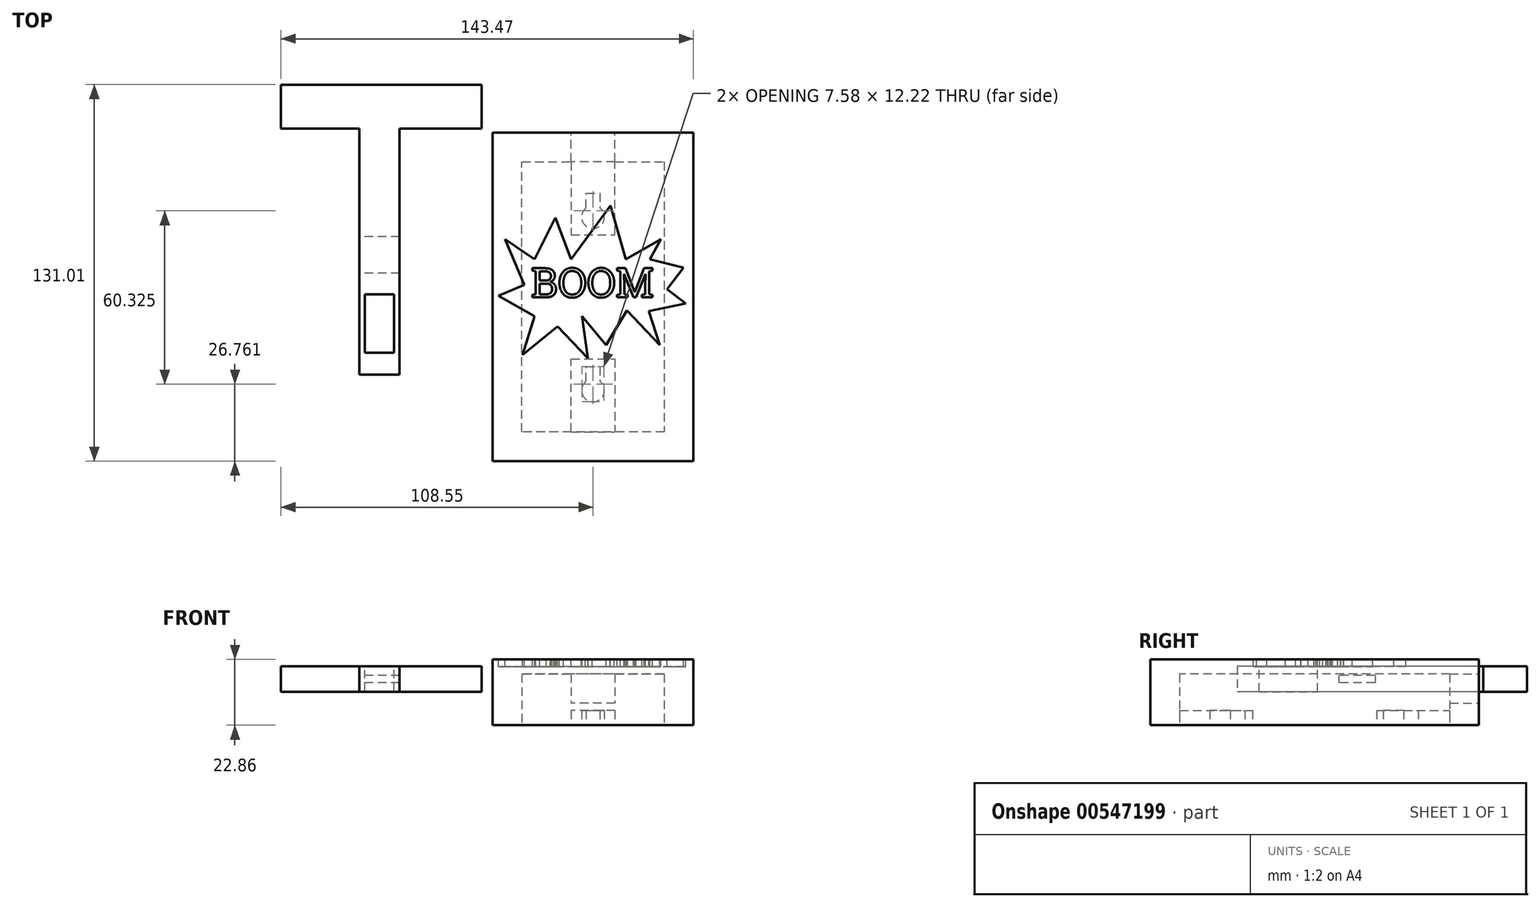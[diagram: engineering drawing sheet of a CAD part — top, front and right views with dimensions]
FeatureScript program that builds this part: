
annotation { "Feature Type Name" : "Feature", "Feature Type Description" : "" }
export const myFeature = defineFeature(function(context is Context, id is Id, definition is map)
    precondition{}
    {
        {
            var Q0;
            Q0=qCreatedBy(makeId("Top.planeOp"),FACE);
            var sketch = newSketch(context, id + "F0", { "sketchPlane" : qUnion([Q0])});
            skCircle(sketch, "E0", {"center": v(0, 34.46) * mm, "radius": 3.97 * mm});
            skCircle(sketch, "E1", {"center": v(0, -25.87) * mm, "radius": 3.97 * mm});
            skLineSegment(sketch, "E2", {"start": v(-34.92, 63.81) * mm, "end": v(34.93, 63.81) * mm});
            skLineSegment(sketch, "E3", {"start": v(34.93, 63.81) * mm, "end": v(34.93, -50.49) * mm});
            skLineSegment(sketch, "E4", {"start": v(34.93, -50.49) * mm, "end": v(-34.92, -50.49) * mm});
            skLineSegment(sketch, "E5", {"start": v(-34.92, -50.49) * mm, "end": v(-34.92, 63.81) * mm});
            skLineSegment(sketch, "E6", {"start": v(-24.76, -40.33) * mm, "end": v(-24.76, 53.65) * mm});
            skLineSegment(sketch, "E7", {"start": v(-24.76, 53.65) * mm, "end": v(24.77, 53.65) * mm});
            skLineSegment(sketch, "E8", {"start": v(24.77, 53.65) * mm, "end": v(24.77, -40.33) * mm});
            skLineSegment(sketch, "E9", {"start": v(24.77, -40.33) * mm, "end": v(-24.76, -40.33) * mm});
            skLineSegment(sketch, "E10", {"start": v(-2.39, 37.63) * mm, "end": v(-2.39, 42.7) * mm});
            skLineSegment(sketch, "E11", {"start": v(2.39, 42.7) * mm, "end": v(2.39, 37.63) * mm});
            skLineSegment(sketch, "E12", {"start": v(-2.39, 42.7) * mm, "end": v(0, 42.7) * mm});
            skLineSegment(sketch, "E13", {"start": v(0, 42.7) * mm, "end": v(2.39, 42.7) * mm});
            skLineSegment(sketch, "E14", {"start": v(-2.39, -22.7) * mm, "end": v(-2.39, -17.62) * mm});
            skLineSegment(sketch, "E15", {"start": v(-2.39, -17.62) * mm, "end": v(0, -17.62) * mm});
            skLineSegment(sketch, "E16", {"start": v(0, -17.62) * mm, "end": v(2.39, -17.62) * mm});
            skLineSegment(sketch, "E17", {"start": v(2.39, -17.62) * mm, "end": v(2.39, -22.7) * mm});
            skLineSegment(sketch, "E18", {"start": v(-7.62, 53.65) * mm, "end": v(-7.62, 28.25) * mm});
            skLineSegment(sketch, "E19", {"start": v(7.62, 28.25) * mm, "end": v(7.62, 53.65) * mm});
            skLineSegment(sketch, "E20", {"start": v(-7.62, 28.25) * mm, "end": v(0, 28.25) * mm});
            skLineSegment(sketch, "E21", {"start": v(0, 28.25) * mm, "end": v(7.62, 28.25) * mm});
            skLineSegment(sketch, "E22", {"start": v(-7.62, -40.33) * mm, "end": v(-7.62, -14.93) * mm});
            skLineSegment(sketch, "E23", {"start": v(-7.62, -14.93) * mm, "end": v(0, -14.93) * mm});
            skLineSegment(sketch, "E24", {"start": v(0, -14.93) * mm, "end": v(7.62, -14.93) * mm});
            skLineSegment(sketch, "E25", {"start": v(7.62, -14.93) * mm, "end": v(7.62, -40.33) * mm});
            skSolve(sketch);
        }
        {
            var Q0;
            Q0=makeQuery(id+"F0.imprint","IMPRINT",FACE,{"disambiguationData":[TD([[makeQuery(id+"F0.imprint","IMPRINT",EDGE,{"derivedFrom":sQuery(id+"F0.wireOp",EDGE,"E2")}),-1.0]])]});
            var Q1;
            {var subQ0=sQuery(id+"F0.wireOp",EDGE,"E14");Q1=makeQuery(id+"F0.imprint","IMPRINT",FACE,{"disambiguationData":[TD([[makeQuery(id+"F0.imprint","IMPRINT",EDGE,{"derivedFrom":subQ0}),1.0]])]});}
            var Q2;
            {var subQ4=sQuery(id+"F0.wireOp",EDGE,"E10");Q2=makeQuery(id+"F0.imprint","IMPRINT",FACE,{"disambiguationData":[TD([[makeQuery(id+"F0.imprint","IMPRINT",EDGE,{"derivedFrom":subQ4}),1.0]])]});}
            extrude(context, id + "F1", {"entities" : qUnion([Q0, Q1, Q2]), "depth" : 5.08 * mm});
        }
        {
            var Q0;
            Q0=makeQuery(id+"F0.imprint","IMPRINT",FACE,{"disambiguationData":[TD([[makeQuery(id+"F0.imprint","IMPRINT",EDGE,{"derivedFrom":sQuery(id+"F0.wireOp",EDGE,"E2")}),-1.0]])]});
            extrude(context, id + "F2", {"entities" : qUnion([Q0]), "operationType" : NewBodyOperationType.ADD, "depth" : 10.16 * mm});
        }
        {
            var Q0;
            Q0=makeQuery(id+"F2.opExtrude","CAP_FACE",FACE,{"disambiguationData":[OSD([sQuery(id+"F0.wireOp",EDGE,"E2"),sQuery(id+"F0.wireOp",EDGE,"E3"),sQuery(id+"F0.wireOp",EDGE,"E4"),sQuery(id+"F0.wireOp",EDGE,"E5"),sQuery(id+"F0.wireOp",EDGE,"E6"),sQuery(id+"F0.wireOp",EDGE,"E7"),sQuery(id+"F0.wireOp",EDGE,"E8"),sQuery(id+"F0.wireOp",EDGE,"E9")])],"isStart":false});
            var sketch = newSketch(context, id + "F3", { "sketchPlane" : qUnion([Q0])});
            skLineSegment(sketch, "E26.0", {"start": v(-34.92, 63.81) * mm, "end": v(34.93, 63.81) * mm});
            skLineSegment(sketch, "E26.1", {"start": v(-34.92, -50.49) * mm, "end": v(-34.92, 63.81) * mm});
            skLineSegment(sketch, "E26.2", {"start": v(34.93, -50.49) * mm, "end": v(-34.92, -50.49) * mm});
            skLineSegment(sketch, "E26.3", {"start": v(34.93, 63.81) * mm, "end": v(34.93, -50.49) * mm});
            skSolve(sketch);
        }
        {
            var Q0;
            Q0=makeQuery(id+"F3.imprint","IMPRINT",FACE,{"disambiguationData":[TD([[makeQuery(id+"F3.imprint","IMPRINT",EDGE,{"derivedFrom":sQuery(id+"F3.wireOp",EDGE,"E26.0")}),-1.0]])]});
            var Q1;
            Q1=makeQuery(id+"F3.imprint","IMPRINT",FACE,{"disambiguationData":[TD([[makeQuery(id+"F3.imprint","IMPRINT",EDGE,{"derivedFrom":makeQuery(id+"F2.opExtrude","CAP_EDGE",EDGE,{"disambiguationData":[OSD([sQuery(id+"F0.wireOp",EDGE,"E6")])],"isStart":false})}),-1.0]])]});
            extrude(context, id + "F4", {"entities" : qUnion([Q0, Q1]), "operationType" : NewBodyOperationType.ADD, "depth" : 12.7 * mm});
        }
        {
            var Q0;
            Q0=makeQuery(id+"F3.imprint","IMPRINT",FACE,{"disambiguationData":[TD([[makeQuery(id+"F3.imprint","IMPRINT",EDGE,{"derivedFrom":sQuery(id+"F3.wireOp",EDGE,"E26.0")}),-1.0]])]});
            var sketch = newSketch(context, id + "F5", { "sketchPlane" : qUnion([Q0])});
            skLineSegment(sketch, "E27.0", {"start": v(-24.76, 53.65) * mm, "end": v(24.77, 53.65) * mm});
            skLineSegment(sketch, "E27.1", {"start": v(-24.76, -40.33) * mm, "end": v(-24.76, 53.65) * mm});
            skLineSegment(sketch, "E27.2", {"start": v(24.77, -40.33) * mm, "end": v(-24.76, -40.33) * mm});
            skLineSegment(sketch, "E27.3", {"start": v(24.77, 53.65) * mm, "end": v(24.77, -40.33) * mm});
            skSolve(sketch);
        }
        {
            var Q0;
            Q0=qSketchRegion(id+"F5",true);
            extrude(context, id + "F6", {"entities" : qUnion([Q0]), "operationType" : NewBodyOperationType.REMOVE, "depth" : 7.62 * mm});
        }
        {
            var Q0;
            {var subQ0=sQuery(id+"F0.wireOp",EDGE,"E2");Q0=makeQuery(id+"F4.boolean.opBoolean","MERGE",FACE,{"derivedFrom":[makeQuery(id+"F2.boolean.opBoolean","MERGE",FACE,{"derivedFrom":[makeQuery(id+"F1.opExtrude","SWEPT_FACE",FACE,{"disambiguationData":[OSD([subQ0])]}),makeQuery(id+"F2.opExtrude","SWEPT_FACE",FACE,{"disambiguationData":[OSD([subQ0])]})]}),makeQuery(id+"F4.opExtrude","SWEPT_FACE",FACE,{"disambiguationData":[OSD([sQuery(id+"F3.wireOp",EDGE,"E26.0")])]})]});}
            var sketch = newSketch(context, id + "F7", { "sketchPlane" : qUnion([Q0])});
            skLineSegment(sketch, "E28.0", {"start": v(34.92, 22.86) * mm, "end": v(-34.93, 22.86) * mm});
            skLineSegment(sketch, "E28.1", {"start": v(-34.93, 22.86) * mm, "end": v(-34.93, 0) * mm});
            skLineSegment(sketch, "E28.2", {"start": v(-34.93, 0) * mm, "end": v(34.92, 0) * mm});
            skLineSegment(sketch, "E28.3", {"start": v(34.92, 22.86) * mm, "end": v(34.92, 0) * mm});
            skLineSegment(sketch, "E29.bottom", {"start": v(-7.62, 17.78) * mm, "end": v(7.62, 17.78) * mm});
            skLineSegment(sketch, "E29.top", {"start": v(-7.62, 7.62) * mm, "end": v(7.62, 7.62) * mm});
            skLineSegment(sketch, "E29.left", {"start": v(-7.62, 17.78) * mm, "end": v(-7.62, 7.62) * mm});
            skLineSegment(sketch, "E29.right", {"start": v(7.62, 17.78) * mm, "end": v(7.62, 7.62) * mm});
            skSolve(sketch);
        }
        {
            var Q0;
            Q0=makeQuery(id+"F7.imprint","IMPRINT",FACE,{"disambiguationData":[TD([[makeQuery(id+"F7.imprint","IMPRINT",EDGE,{"derivedFrom":sQuery(id+"F7.wireOp",EDGE,"E29.bottom")}),-1.0]])]});
            extrude(context, id + "F8", {"entities" : qUnion([Q0]), "operationType" : NewBodyOperationType.REMOVE, "oppositeDirection" : true, "depth" : 25.4 * mm});
        }
        {
            var Q0;
            Q0=makeQuery(id+"F4.opExtrude","CAP_FACE",FACE,{"disambiguationData":[OSD([sQuery(id+"F3.wireOp",EDGE,"E26.0"),sQuery(id+"F3.wireOp",EDGE,"E26.1"),sQuery(id+"F3.wireOp",EDGE,"E26.2"),sQuery(id+"F3.wireOp",EDGE,"E26.3")])],"isStart":false});
            var sketch = newSketch(context, id + "F9", { "sketchPlane" : qUnion([Q0])});
            skText(sketch, "E30", { "text": "BOOM", "fontName": "RobotoSlab-Regular.ttf"});
            skPoint(sketch, "E31", {"position": v(21.59, 11.64) * mm});
            skLineSegment(sketch, "E32", {"start": v(-12.28, -3.6) * mm, "end": v(-24.5, -13.53) * mm});
            skLineSegment(sketch, "E33", {"start": v(-24.5, -13.53) * mm, "end": v(-20.3, 0) * mm});
            skLineSegment(sketch, "E34", {"start": v(-20.3, 0) * mm, "end": v(-32.9, 7.1) * mm});
            skLineSegment(sketch, "E35", {"start": v(-32.9, 7.1) * mm, "end": v(-23.93, 10.91) * mm});
            skLineSegment(sketch, "E36", {"start": v(-23.93, 10.91) * mm, "end": v(-30.66, 26.73) * mm});
            skLineSegment(sketch, "E37", {"start": v(-30.66, 26.73) * mm, "end": v(-20.3, 19.7) * mm});
            skLineSegment(sketch, "E38", {"start": v(-20.3, 19.7) * mm, "end": v(-13.04, 34.2) * mm});
            skLineSegment(sketch, "E39", {"start": v(-13.04, 34.2) * mm, "end": v(-7.7, 19.7) * mm});
            skLineSegment(sketch, "E40", {"start": v(-7.7, 19.7) * mm, "end": v(6.05, 38.4) * mm});
            skLineSegment(sketch, "E41", {"start": v(6.05, 38.4) * mm, "end": v(11.4, 19.7) * mm});
            skLineSegment(sketch, "E42", {"start": v(11.4, 19.7) * mm, "end": v(23.62, 26.73) * mm});
            skLineSegment(sketch, "E43", {"start": v(23.62, 26.73) * mm, "end": v(19.8, 19.7) * mm});
            skLineSegment(sketch, "E44", {"start": v(19.8, 19.7) * mm, "end": v(31.45, 16.78) * mm});
            skLineSegment(sketch, "E45", {"start": v(31.45, 16.78) * mm, "end": v(25.72, 9.38) * mm});
            skLineSegment(sketch, "E46", {"start": v(25.72, 9.38) * mm, "end": v(32.25, 4.33) * mm});
            skLineSegment(sketch, "E47", {"start": v(32.25, 4.33) * mm, "end": v(19.42, 1.74) * mm});
            skLineSegment(sketch, "E48", {"start": v(19.42, 1.74) * mm, "end": v(23.24, -10.1) * mm});
            skLineSegment(sketch, "E49", {"start": v(23.24, -10.1) * mm, "end": v(11.78, 1.94) * mm});
            skLineSegment(sketch, "E50", {"start": v(11.78, 1.94) * mm, "end": v(4.52, -10.1) * mm});
            skLineSegment(sketch, "E51", {"start": v(4.52, -10.1) * mm, "end": v(-3.88, 0) * mm});
            skLineSegment(sketch, "E52", {"start": v(-3.88, 0) * mm, "end": v(-1.78, -14.68) * mm});
            skLineSegment(sketch, "E53", {"start": v(-1.78, -14.68) * mm, "end": v(-12.28, -3.6) * mm});
            const initialGuessF9  = {"E30": [-0.0216, 0.0065, 1, 0, 0.01027]};
            skSetInitialGuess(sketch, initialGuessF9);
            skSolve(sketch);
        }
        {
            var Q0;
            Q0=qSketchRegion(id+"F9",true);
            extrude(context, id + "F10", {"entities" : qUnion([Q0]), "operationType" : NewBodyOperationType.REMOVE, "oppositeDirection" : true, "depth" : 2.54 * mm});
        }
        {
            var Q0;
            Q0=makeQuery(id+"F9.imprint","IMPRINT",FACE,{"disambiguationData":[TD([[makeQuery(id+"F9.imprint","IMPRINT",EDGE,{"derivedFrom":sQuery(id+"F9.wireOp",EDGE,"E30.sketch_text.stroke-40")}),1.0]])]});
            var Q1;
            Q1=makeQuery(id+"F9.imprint","IMPRINT",FACE,{"disambiguationData":[TD([[makeQuery(id+"F9.imprint","IMPRINT",EDGE,{"derivedFrom":sQuery(id+"F9.wireOp",EDGE,"E30.sketch_text.stroke-60")}),1.0]])]});
            var Q2;
            Q2=makeQuery(id+"F9.imprint","IMPRINT",FACE,{"disambiguationData":[TD([[makeQuery(id+"F9.imprint","IMPRINT",EDGE,{"derivedFrom":sQuery(id+"F9.wireOp",EDGE,"E30.sketch_text.stroke-23")}),1.0]])]});
            var Q3;
            Q3=makeQuery(id+"F9.imprint","IMPRINT",FACE,{"disambiguationData":[TD([[makeQuery(id+"F9.imprint","IMPRINT",EDGE,{"derivedFrom":sQuery(id+"F9.wireOp",EDGE,"E30.sketch_text.stroke-16")}),1.0]])]});
            extrude(context, id + "F11", {"entities" : qUnion([Q0, Q1, Q2, Q3]), "operationType" : NewBodyOperationType.REMOVE, "oppositeDirection" : true, "depth" : 2.54 * mm});
        }
        {
            var Q0;
            Q0=qCreatedBy(makeId("Front.planeOp"),FACE);
            var sketch = newSketch(context, id + "F12", { "sketchPlane" : qUnion([Q0])});
            skLineSegment(sketch, "E54.bottom", {"start": v(-67.27, 20.54) * mm, "end": v(-81.24, 20.54) * mm});
            skLineSegment(sketch, "E54.top", {"start": v(-67.27, 11.65) * mm, "end": v(-81.24, 11.65) * mm});
            skLineSegment(sketch, "E54.left", {"start": v(-67.27, 20.54) * mm, "end": v(-67.27, 11.65) * mm});
            skLineSegment(sketch, "E54.right", {"start": v(-81.24, 20.54) * mm, "end": v(-81.24, 11.65) * mm});
            skSolve(sketch);
        }
        {
            var Q0;
            Q0=makeQuery(id+"F12.imprint","IMPRINT",FACE,{"disambiguationData":[TD([[makeQuery(id+"F12.imprint","IMPRINT",EDGE,{"derivedFrom":sQuery(id+"F12.wireOp",EDGE,"E54.bottom")}),1.0]])]});
            extrude(context, id + "F13", {"entities" : qUnion([Q0]), "oppositeDirection" : true, "depth" : 65.28 * mm});
        }
        {
            var Q0;
            Q0=makeQuery(id+"F13.opExtrude","CAP_FACE",FACE,{"disambiguationData":[OSD([sQuery(id+"F12.wireOp",EDGE,"E54.bottom"),sQuery(id+"F12.wireOp",EDGE,"E54.top"),sQuery(id+"F12.wireOp",EDGE,"E54.left"),sQuery(id+"F12.wireOp",EDGE,"E54.right")])],"isStart":true});
            extrude(context, id + "F14", {"entities" : qUnion([Q0]), "operationType" : NewBodyOperationType.ADD, "depth" : 20.32 * mm});
        }
        {
            var Q0;
            {var subQ0=sQuery(id+"F12.wireOp",EDGE,"E54.bottom");Q0=makeQuery(id+"F14.boolean.opBoolean","MERGE",FACE,{"derivedFrom":[makeQuery(id+"F13.opExtrude","SWEPT_FACE",FACE,{"disambiguationData":[OSD([subQ0])]}),makeQuery(id+"F14.opExtrude","SWEPT_FACE",FACE,{"disambiguationData":[OSD([subQ0])]})]});}
            var sketch = newSketch(context, id + "F15", { "sketchPlane" : qUnion([Q0])});
            skLineSegment(sketch, "E55", {"start": v(-79.34, 7.62) * mm, "end": v(-79.34, -12.7) * mm});
            skLineSegment(sketch, "E56", {"start": v(-79.34, -12.7) * mm, "end": v(-69.18, -12.7) * mm});
            skLineSegment(sketch, "E57", {"start": v(-69.18, -12.7) * mm, "end": v(-69.18, 7.62) * mm});
            skLineSegment(sketch, "E58", {"start": v(-69.18, 7.62) * mm, "end": v(-79.34, 7.62) * mm});
            skLineSegment(sketch, "E59.0", {"start": v(-67.27, 65.28) * mm, "end": v(-81.24, 65.28) * mm});
            skSolve(sketch);
        }
        {
            var Q0;
            Q0=makeQuery(id+"F15.imprint","IMPRINT",FACE,{"disambiguationData":[TD([[makeQuery(id+"F15.imprint","IMPRINT",EDGE,{"derivedFrom":sQuery(id+"F15.wireOp",EDGE,"E55")}),1.0]])]});
            extrude(context, id + "F16", {"entities" : qUnion([Q0]), "operationType" : NewBodyOperationType.REMOVE, "oppositeDirection" : true, "depth" : 25.4 * mm});
        }
        {
            var Q0;
            Q0=makeQuery(id+"F13.opExtrude","CAP_FACE",FACE,{"disambiguationData":[OSD([sQuery(id+"F12.wireOp",EDGE,"E54.bottom"),sQuery(id+"F12.wireOp",EDGE,"E54.top"),sQuery(id+"F12.wireOp",EDGE,"E54.left"),sQuery(id+"F12.wireOp",EDGE,"E54.right")])],"isStart":false});
            var sketch = newSketch(context, id + "F17", { "sketchPlane" : qUnion([Q0])});
            skLineSegment(sketch, "E60", {"start": v(38.7, 20.54) * mm, "end": v(108.55, 20.54) * mm});
            skLineSegment(sketch, "E61", {"start": v(108.55, 20.54) * mm, "end": v(108.55, 11.65) * mm});
            skLineSegment(sketch, "E62", {"start": v(108.55, 11.65) * mm, "end": v(38.7, 11.65) * mm});
            skLineSegment(sketch, "E63", {"start": v(38.7, 11.65) * mm, "end": v(38.7, 20.54) * mm});
            skSolve(sketch);
        }
        {
            var Q0;
            {var subQ2=sQuery(id+"F17.wireOp",EDGE,"E63");Q0=makeQuery(id+"F17.imprint","IMPRINT",FACE,{"disambiguationData":[TD([[makeQuery(id+"F17.imprint","IMPRINT",EDGE,{"derivedFrom":subQ2}),-1.0]])]});}
            var Q1;
            {var subQ1=makeQuery(id+"F13.opExtrude","CAP_EDGE",EDGE,{"disambiguationData":[OSD([sQuery(id+"F12.wireOp",EDGE,"E54.left")])],"isStart":false});Q1=makeQuery(id+"F17.imprint","IMPRINT",FACE,{"disambiguationData":[TD([[makeQuery(id+"F17.imprint","IMPRINT",EDGE,{"derivedFrom":subQ1}),1.0]])]});}
            var Q2;
            {var subQ2=sQuery(id+"F17.wireOp",EDGE,"E61");Q2=makeQuery(id+"F17.imprint","IMPRINT",FACE,{"disambiguationData":[TD([[makeQuery(id+"F17.imprint","IMPRINT",EDGE,{"derivedFrom":subQ2}),-1.0]])]});}
            extrude(context, id + "F18", {"entities" : qUnion([Q0, Q1, Q2]), "operationType" : NewBodyOperationType.ADD, "depth" : 15.24 * mm});
        }
        {
            var Q0;
            {var subQ0=sQuery(id+"F12.wireOp",EDGE,"E54.right");Q0=makeQuery(id+"F14.boolean.opBoolean","MERGE",FACE,{"derivedFrom":[makeQuery(id+"F13.opExtrude","SWEPT_FACE",FACE,{"disambiguationData":[OSD([subQ0])]}),makeQuery(id+"F14.opExtrude","SWEPT_FACE",FACE,{"disambiguationData":[OSD([subQ0])]})]});}
            var sketch = newSketch(context, id + "F19", { "sketchPlane" : qUnion([Q0])});
            skLineSegment(sketch, "E64.bottom", {"start": v(-27.63, 17.3) * mm, "end": v(-14.93, 17.3) * mm});
            skLineSegment(sketch, "E64.top", {"start": v(-27.63, 14.77) * mm, "end": v(-14.93, 14.77) * mm});
            skLineSegment(sketch, "E64.left", {"start": v(-27.63, 17.3) * mm, "end": v(-27.63, 14.77) * mm});
            skLineSegment(sketch, "E64.right", {"start": v(-14.93, 17.3) * mm, "end": v(-14.93, 14.77) * mm});
            skSolve(sketch);
        }
        {
            var Q0;
            Q0=makeQuery(id+"F19.imprint","IMPRINT",FACE,{"disambiguationData":[TD([[makeQuery(id+"F19.imprint","IMPRINT",EDGE,{"derivedFrom":sQuery(id+"F19.wireOp",EDGE,"E64.bottom")}),-1.0]])]});
            extrude(context, id + "F20", {"entities" : qUnion([Q0]), "operationType" : NewBodyOperationType.REMOVE, "oppositeDirection" : true, "depth" : 25.4 * mm, "offsetDistance" : 25.4 * mm});
        }
    });
